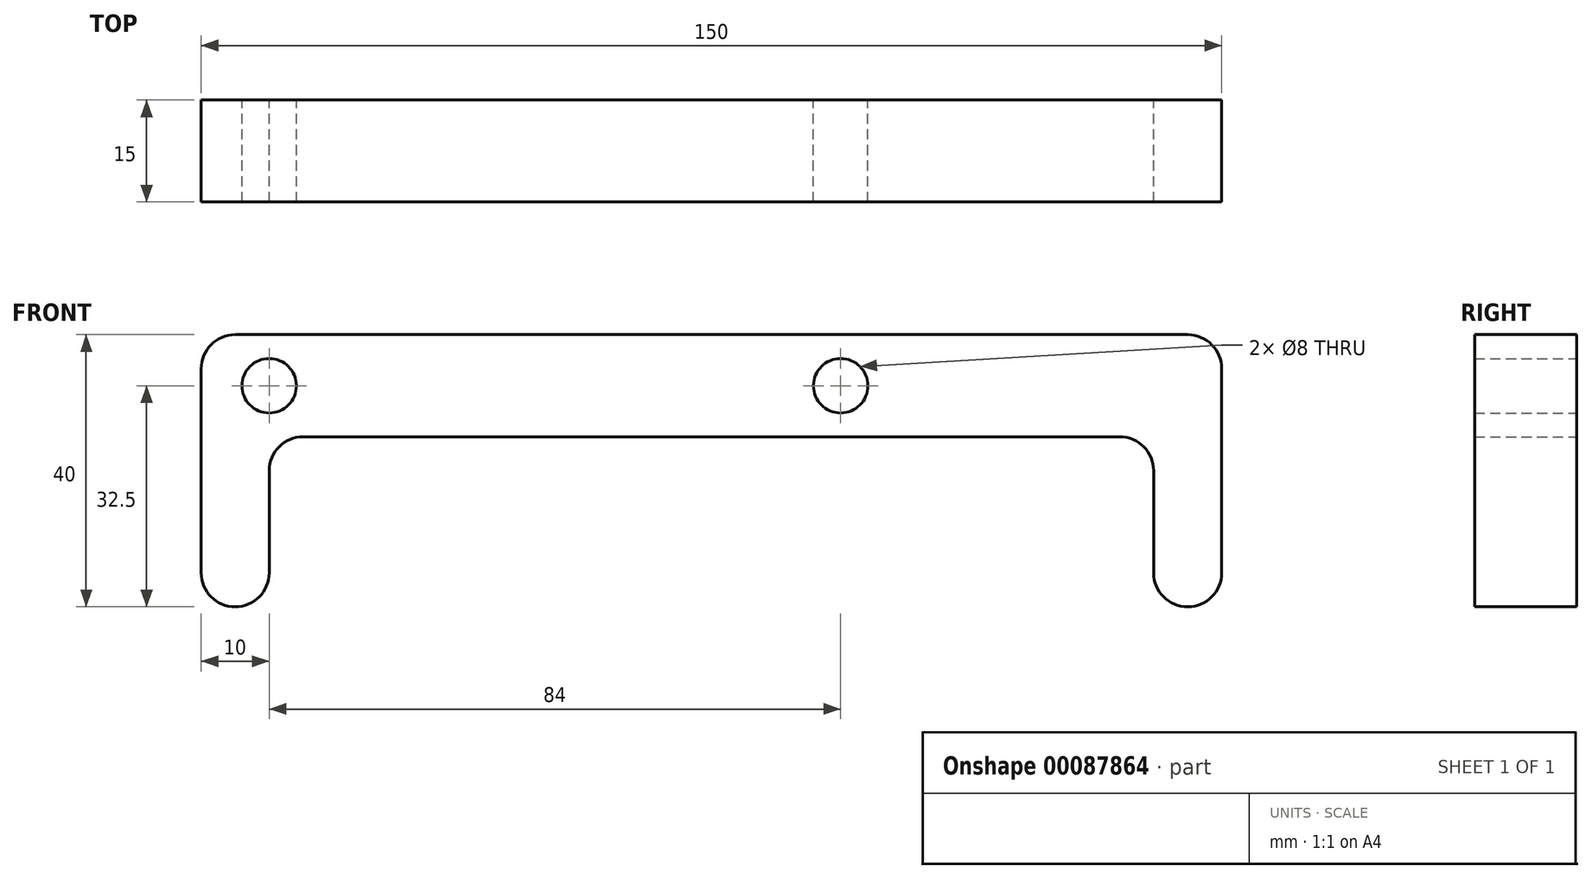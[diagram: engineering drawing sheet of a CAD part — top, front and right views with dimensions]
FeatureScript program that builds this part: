
annotation { "Feature Type Name" : "Feature", "Feature Type Description" : "" }
export const myFeature = defineFeature(function(context is Context, id is Id, definition is map)
    precondition{}
    {
        {
            var Q0;
            Q0=qCreatedBy(makeId("Front.planeOp"),FACE);
            var sketch = newSketch(context, id + "F0", { "sketchPlane" : qUnion([Q0])});
            skCircle(sketch, "E0", {"center": v(0, 0) * mm, "radius": 4 * mm});
            skCircle(sketch, "E1", {"center": v(-84, 0) * mm, "radius": 4 * mm});
            skLineSegment(sketch, "E2.bottom", {"start": v(-94, 7.5) * mm, "end": v(56, 7.5) * mm});
            skLineSegment(sketch, "E2.top", {"start": v(-94, -7.5) * mm, "end": v(56, -7.5) * mm});
            skLineSegment(sketch, "E2.left", {"start": v(-94, 7.5) * mm, "end": v(-94, -7.5) * mm});
            skLineSegment(sketch, "E2.right", {"start": v(56, 7.5) * mm, "end": v(56, -7.5) * mm});
            skLineSegment(sketch, "E3.bottom", {"start": v(-94, -7.5) * mm, "end": v(-84, -7.5) * mm});
            skLineSegment(sketch, "E3.top", {"start": v(-94, -32.5) * mm, "end": v(-84, -32.5) * mm});
            skLineSegment(sketch, "E3.left", {"start": v(-94, -7.5) * mm, "end": v(-94, -32.5) * mm});
            skLineSegment(sketch, "E3.right", {"start": v(-84, -7.5) * mm, "end": v(-84, -32.5) * mm});
            skLineSegment(sketch, "E4.bottom", {"start": v(56, -7.5) * mm, "end": v(46, -7.5) * mm});
            skLineSegment(sketch, "E4.top", {"start": v(56, -32.5) * mm, "end": v(46, -32.5) * mm});
            skLineSegment(sketch, "E4.left", {"start": v(56, -7.5) * mm, "end": v(56, -32.5) * mm});
            skLineSegment(sketch, "E4.right", {"start": v(46, -7.5) * mm, "end": v(46, -32.5) * mm});
            skSolve(sketch);
        }
        {
            var Q0;
            Q0 = qSketchRegion(id + "F0", true);
            extrude(context, id + "F1", {"entities" : qUnion([Q0]), "depth" : 15 * mm});
        }
        {
            var Q0;
            Q0=makeQuery(id+"F1.opExtrude","SWEPT_EDGE",EDGE,{"disambiguationData":[OSD([sQuery(id+"F0.wireOp",EDGE,"E2.top"),sQuery(id+"F0.wireOp",EDGE,"E3.bottom"),sQuery(id+"F0.wireOp",EDGE,"E3.right")])]});
            var Q1;
            Q1=makeQuery(id+"F1.opExtrude","SWEPT_EDGE",EDGE,{"disambiguationData":[OSD([sQuery(id+"F0.wireOp",EDGE,"E2.top"),sQuery(id+"F0.wireOp",EDGE,"E4.bottom"),sQuery(id+"F0.wireOp",EDGE,"E4.right")])]});
            var Q2;
            Q2=makeQuery(id+"F1.opExtrude","SWEPT_EDGE",EDGE,{"disambiguationData":[OSD([sQuery(id+"F0.wireOp",EDGE,"E2.bottom"),sQuery(id+"F0.wireOp",EDGE,"E2.right")])]});
            var Q3;
            Q3=makeQuery(id+"F1.opExtrude","SWEPT_EDGE",EDGE,{"disambiguationData":[OSD([sQuery(id+"F0.wireOp",EDGE,"E4.top"),sQuery(id+"F0.wireOp",EDGE,"E4.left")])]});
            var Q4;
            Q4=makeQuery(id+"F1.opExtrude","SWEPT_EDGE",EDGE,{"disambiguationData":[OSD([sQuery(id+"F0.wireOp",EDGE,"E4.top"),sQuery(id+"F0.wireOp",EDGE,"E4.right")])]});
            var Q5;
            Q5=makeQuery(id+"F1.opExtrude","SWEPT_EDGE",EDGE,{"disambiguationData":[OSD([sQuery(id+"F0.wireOp",EDGE,"E3.top"),sQuery(id+"F0.wireOp",EDGE,"E3.left")])]});
            var Q6;
            Q6=makeQuery(id+"F1.opExtrude","SWEPT_EDGE",EDGE,{"disambiguationData":[OSD([sQuery(id+"F0.wireOp",EDGE,"E3.top"),sQuery(id+"F0.wireOp",EDGE,"E3.right")])]});
            var Q7;
            Q7=makeQuery(id+"F1.opExtrude","SWEPT_EDGE",EDGE,{"disambiguationData":[OSD([sQuery(id+"F0.wireOp",EDGE,"E2.bottom"),sQuery(id+"F0.wireOp",EDGE,"E2.left")])]});
            fillet(context, id + "F2", {"entities" : qUnion([Q0, Q1, Q2, Q3, Q4, Q5, Q6, Q7]), "radius" : 5 * mm, "tangentPropagation" : true, "allowEdgeOverflow" : false});
        }
    });
